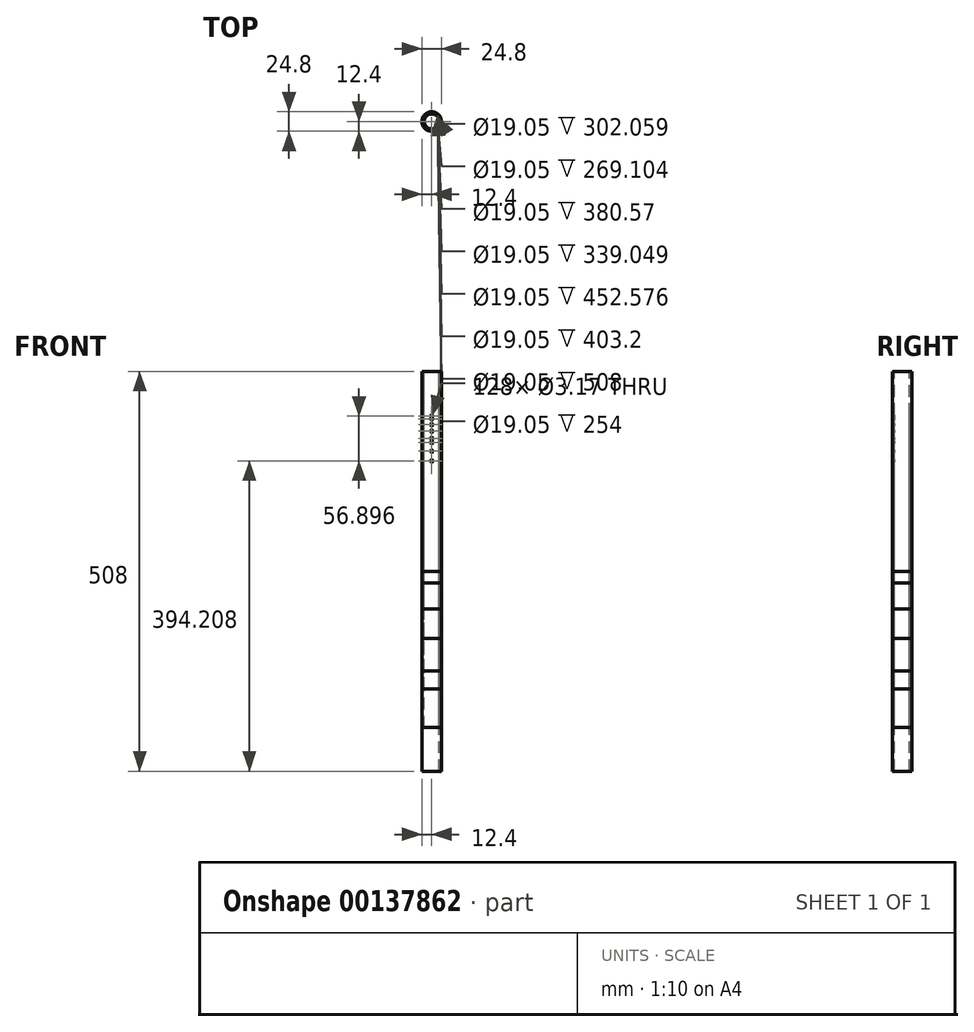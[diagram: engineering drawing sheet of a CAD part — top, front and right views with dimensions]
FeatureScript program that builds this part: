
annotation { "Feature Type Name" : "Feature", "Feature Type Description" : "" }
export const myFeature = defineFeature(function(context is Context, id is Id, definition is map)
    precondition{}
    {
        {
            var Q0;
            Q0=qCreatedBy(makeId("Top.planeOp"),FACE);
            var sketch = newSketch(context, id + "F0", { "sketchPlane" : qUnion([Q0])});
            skCircle(sketch, "E0", {"center": v(0, 0) * mm, "radius": 9.52 * mm});
            skCircle(sketch, "E1", {"center": v(0, 0) * mm, "radius": 12.4 * mm});
            skSolve(sketch);
        }
        {
            var Q0;
            Q0=qSketchRegion(id+"F0",true);
            extrude(context, id + "F1", {"entities" : qUnion([Q0]), "oppositeDirection" : true, "depth" : 508 * mm});
        }
        {
            var Q0;
            Q0=qSketchRegion(id+"F0",true);
            extrude(context, id + "F2", {"entities" : qUnion([Q0]), "oppositeDirection" : true, "depth" : 452.58 * mm});
        }
        {
            var Q0;
            Q0=qSketchRegion(id+"F0",true);
            extrude(context, id + "F3", {"entities" : qUnion([Q0]), "oppositeDirection" : true, "depth" : 403.2 * mm});
        }
        {
            var Q0;
            Q0=qSketchRegion(id+"F0",true);
            extrude(context, id + "F4", {"entities" : qUnion([Q0]), "oppositeDirection" : true, "depth" : 380.57 * mm});
        }
        {
            var Q0;
            Q0=qSketchRegion(id+"F0",true);
            extrude(context, id + "F5", {"entities" : qUnion([Q0]), "oppositeDirection" : true, "depth" : 339.05 * mm});
        }
        {
            var Q0;
            Q0=qSketchRegion(id+"F0",true);
            extrude(context, id + "F6", {"entities" : qUnion([Q0]), "oppositeDirection" : true, "depth" : 302.06 * mm});
        }
        {
            var Q0;
            Q0=qSketchRegion(id+"F0",true);
            extrude(context, id + "F7", {"entities" : qUnion([Q0]), "oppositeDirection" : true, "depth" : 269.1 * mm});
        }
        {
            var Q0;
            Q0=qSketchRegion(id+"F0",true);
            extrude(context, id + "F8", {"entities" : qUnion([Q0]), "oppositeDirection" : true, "depth" : 254 * mm});
        }
        {
            var Q0;
            Q0=qCreatedBy(makeId("Front.planeOp"),FACE);
            var sketch = newSketch(context, id + "F9", { "sketchPlane" : qUnion([Q0])});
            skCircle(sketch, "E2", {"center": v(0, -56.9) * mm, "radius": 1.59 * mm});
            skCircle(sketch, "E3", {"center": v(0, -60.23) * mm, "radius": 1.59 * mm});
            skCircle(sketch, "E4", {"center": v(0, -67.66) * mm, "radius": 1.59 * mm});
            skCircle(sketch, "E5", {"center": v(0, -75.95) * mm, "radius": 1.59 * mm});
            skCircle(sketch, "E6", {"center": v(0, -85.25) * mm, "radius": 1.59 * mm});
            skCircle(sketch, "E7", {"center": v(0, -90.32) * mm, "radius": 1.59 * mm});
            skCircle(sketch, "E8", {"center": v(0, -101.38) * mm, "radius": 1.59 * mm});
            skCircle(sketch, "E9", {"center": v(0, -113.8) * mm, "radius": 1.59 * mm});
            skSolve(sketch);
        }
        {
            var Q0;
            Q0=makeQuery(id+"F9.imprint","IMPRINT",FACE,{"disambiguationData":[TD([[makeQuery(id+"F9.imprint","IMPRINT",EDGE,{"derivedFrom":sQuery(id+"F9.wireOp",EDGE,"E9")}),1.0]])]});
            extrude(context, id + "F10", {"entities" : qUnion([Q0]), "operationType" : NewBodyOperationType.REMOVE, "endBound" : BoundingType.THROUGH_ALL, "oppositeDirection" : true, "depth" : 25.4 * mm, "hasSecondDirection" : true, "secondDirectionBound" : SecondDirectionBoundingType.THROUGH_ALL, "secondDirectionOppositeDirection" : false, "secondDirectionDepth" : 25.4 * mm});
        }
        {
            var Q0;
            Q0=makeQuery(id+"F9.imprint","IMPRINT",FACE,{"disambiguationData":[TD([[makeQuery(id+"F9.imprint","IMPRINT",EDGE,{"derivedFrom":sQuery(id+"F9.wireOp",EDGE,"E8")}),1.0]])]});
            extrude(context, id + "F11", {"entities" : qUnion([Q0]), "operationType" : NewBodyOperationType.REMOVE, "endBound" : BoundingType.THROUGH_ALL, "oppositeDirection" : true, "depth" : 25.4 * mm, "hasSecondDirection" : true, "secondDirectionBound" : SecondDirectionBoundingType.THROUGH_ALL, "secondDirectionOppositeDirection" : false, "secondDirectionDepth" : 25.4 * mm});
        }
        {
            var Q0;
            Q0=makeQuery(id+"F9.imprint","IMPRINT",FACE,{"disambiguationData":[TD([[makeQuery(id+"F9.imprint","IMPRINT",EDGE,{"derivedFrom":sQuery(id+"F9.wireOp",EDGE,"E7")}),1.0]])]});
            extrude(context, id + "F12", {"entities" : qUnion([Q0]), "operationType" : NewBodyOperationType.REMOVE, "endBound" : BoundingType.THROUGH_ALL, "oppositeDirection" : true, "depth" : 25.4 * mm, "hasSecondDirection" : true, "secondDirectionBound" : SecondDirectionBoundingType.THROUGH_ALL, "secondDirectionOppositeDirection" : false, "secondDirectionDepth" : 25.4 * mm});
        }
        {
            var Q0;
            Q0=makeQuery(id+"F9.imprint","IMPRINT",FACE,{"disambiguationData":[TD([[makeQuery(id+"F9.imprint","IMPRINT",EDGE,{"derivedFrom":sQuery(id+"F9.wireOp",EDGE,"E6")}),1.0]])]});
            extrude(context, id + "F13", {"entities" : qUnion([Q0]), "operationType" : NewBodyOperationType.REMOVE, "endBound" : BoundingType.THROUGH_ALL, "oppositeDirection" : true, "depth" : 25.4 * mm, "hasSecondDirection" : true, "secondDirectionBound" : SecondDirectionBoundingType.THROUGH_ALL, "secondDirectionOppositeDirection" : false, "secondDirectionDepth" : 25.4 * mm});
        }
        {
            var Q0;
            Q0=makeQuery(id+"F9.imprint","IMPRINT",FACE,{"disambiguationData":[TD([[makeQuery(id+"F9.imprint","IMPRINT",EDGE,{"derivedFrom":sQuery(id+"F9.wireOp",EDGE,"E5")}),1.0]])]});
            extrude(context, id + "F14", {"entities" : qUnion([Q0]), "operationType" : NewBodyOperationType.REMOVE, "endBound" : BoundingType.THROUGH_ALL, "oppositeDirection" : true, "depth" : 25.4 * mm, "hasSecondDirection" : true, "secondDirectionBound" : SecondDirectionBoundingType.THROUGH_ALL, "secondDirectionOppositeDirection" : false, "secondDirectionDepth" : 25.4 * mm});
        }
        {
            var Q0;
            Q0=makeQuery(id+"F9.imprint","IMPRINT",FACE,{"disambiguationData":[TD([[makeQuery(id+"F9.imprint","IMPRINT",EDGE,{"derivedFrom":sQuery(id+"F9.wireOp",EDGE,"E4")}),1.0]])]});
            extrude(context, id + "F15", {"entities" : qUnion([Q0]), "operationType" : NewBodyOperationType.REMOVE, "endBound" : BoundingType.THROUGH_ALL, "oppositeDirection" : true, "depth" : 25.4 * mm, "hasSecondDirection" : true, "secondDirectionBound" : SecondDirectionBoundingType.THROUGH_ALL, "secondDirectionOppositeDirection" : false, "secondDirectionDepth" : 25.4 * mm});
        }
        {
            var Q0;
            Q0=makeQuery(id+"F9.imprint","IMPRINT",FACE,{"disambiguationData":[TD([[makeQuery(id+"F9.imprint","IMPRINT",EDGE,{"derivedFrom":sQuery(id+"F9.wireOp",EDGE,"E3")}),1.0]])]});
            extrude(context, id + "F16", {"entities" : qUnion([Q0]), "operationType" : NewBodyOperationType.REMOVE, "endBound" : BoundingType.THROUGH_ALL, "oppositeDirection" : true, "depth" : 25.4 * mm, "hasSecondDirection" : true, "secondDirectionBound" : SecondDirectionBoundingType.THROUGH_ALL, "secondDirectionOppositeDirection" : false, "secondDirectionDepth" : 25.4 * mm});
        }
        {
            var Q0;
            Q0=makeQuery(id+"F9.imprint","IMPRINT",FACE,{"disambiguationData":[TD([[makeQuery(id+"F9.imprint","IMPRINT",EDGE,{"derivedFrom":sQuery(id+"F9.wireOp",EDGE,"E2")}),1.0]])]});
            extrude(context, id + "F17", {"entities" : qUnion([Q0]), "operationType" : NewBodyOperationType.REMOVE, "endBound" : BoundingType.THROUGH_ALL, "oppositeDirection" : true, "depth" : 25.4 * mm, "hasSecondDirection" : true, "secondDirectionBound" : SecondDirectionBoundingType.THROUGH_ALL, "secondDirectionOppositeDirection" : false, "secondDirectionDepth" : 25.4 * mm});
        }
    });
